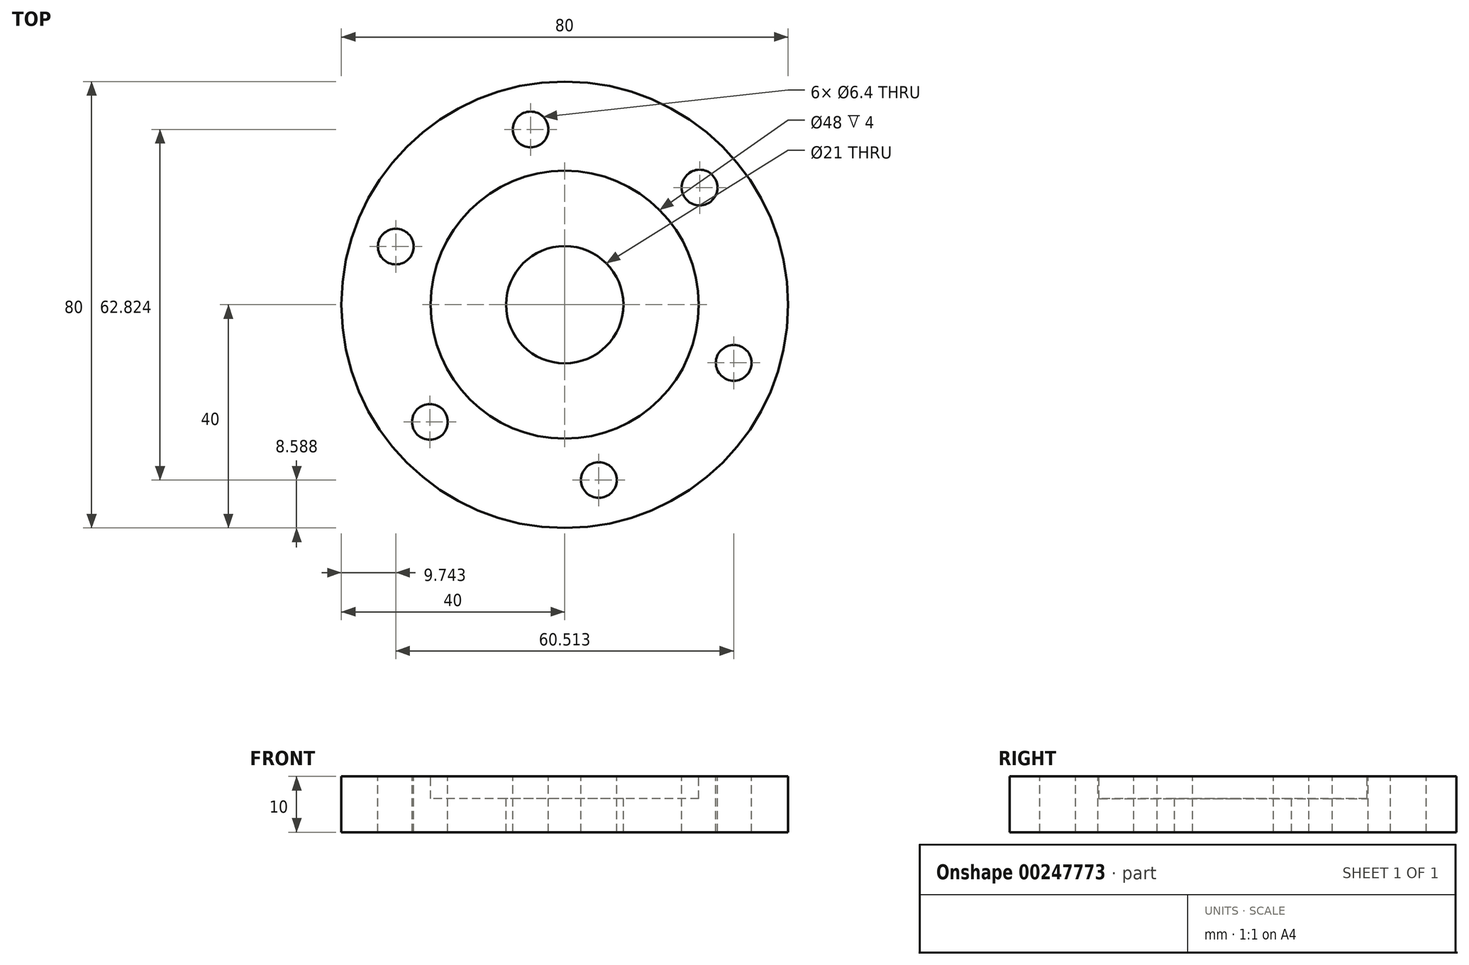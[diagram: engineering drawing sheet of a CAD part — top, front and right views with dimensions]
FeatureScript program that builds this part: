
annotation { "Feature Type Name" : "Feature", "Feature Type Description" : "" }
export const myFeature = defineFeature(function(context is Context, id is Id, definition is map)
    precondition{}
    {
        {
            var Q0;
            Q0=qCreatedBy(makeId("Top.planeOp"),FACE);
            var sketch = newSketch(context, id + "F0", { "sketchPlane" : qUnion([Q0])});
            skCircle(sketch, "E0", {"center": v(0, 0) * mm, "radius": 40 * mm});
            skLineSegment(sketch, "E1", {"start": v(0, 0) * mm, "end": v(-9.46, 48.68) * mm, "construction": true});
            skCircle(sketch, "E2", {"center": v(0, 0) * mm, "radius": 32 * mm, "construction": true});
            skPoint(sketch, "E3", {"position": v(-6.1, 31.41) * mm});
            skPoint(sketch, "E4.1.0", {"position": v(-30.26, 10.42) * mm});
            skPoint(sketch, "E4.2.0", {"position": v(-24.15, -21) * mm});
            skPoint(sketch, "E4.3.0", {"position": v(6.1, -31.41) * mm});
            skPoint(sketch, "E4.4.0", {"position": v(30.26, -10.42) * mm});
            skPoint(sketch, "E4.5.0", {"position": v(24.15, 21) * mm});
            skSolve(sketch);
        }
        {
            var Q0;
            Q0=qSketchRegion(id+"F0",true);
            extrude(context, id + "F1", {"entities" : qUnion([Q0]), "oppositeDirection" : true, "depth" : 10 * mm});
        }
        {
            var Q0;
            Q0=qCreatedBy(makeId("Top.planeOp"),FACE);
            var sketch = newSketch(context, id + "F2", { "sketchPlane" : qUnion([Q0])});
            skCircle(sketch, "E5", {"center": v(0, 0) * mm, "radius": 24 * mm});
            skSolve(sketch);
        }
        {
            var Q0;
            Q0=qSketchRegion(id+"F2",true);
            extrude(context, id + "F3", {"entities" : qUnion([Q0]), "operationType" : NewBodyOperationType.REMOVE, "oppositeDirection" : true, "depth" : 4 * mm, "hasSecondDirection" : true, "secondDirectionOppositeDirection" : false, "secondDirectionDepth" : 10 * mm});
        }
        {
            var Q0;
            Q0=makeQuery(id+"F3.boolean.opBoolean","COPY",FACE,{"derivedFrom":makeQuery(id+"F3.opExtrude","CAP_FACE",FACE,{"disambiguationData":[OSD([sQuery(id+"F2.wireOp",EDGE,"E5")])],"isStart":false})});
            cPlane(context, id + "F4", {"entities" : qUnion([Q0]), "cplaneType" : CPlaneType.OFFSET, "offset" : 0 * mm, "width" : 150 * mm, "height" : 150 * mm});
        }
        {
            var Q0;
            Q0=qCreatedBy(id+"F4.planeOp",FACE);
            var sketch = newSketch(context, id + "F5", { "sketchPlane" : qUnion([Q0])});
            skPoint(sketch, "E6", {"position": v(0, 0) * mm});
            skSolve(sketch);
        }
        {
            var Q0;
            Q0=sQuery(id+"F5.wireOp",VERTEX,"E6");
            var Q1;
            Q1=makeQuery(id+"F1.opExtrude","SWEPT_BODY",BODY,{"disambiguationData":[OSD([sQuery(id+"F0.wireOp",EDGE,"E0")])]});
            hole(context, id + "F6", {"style" : HoleStyle.SIMPLE, "endStyle" : HoleEndStyle.THROUGH, "holeDiameter" : 21 * mm, "locations" : qUnion([Q0]), "scope" : qUnion([Q1]), "isTappedThrough" : true});
        }
        {
            var Q0;
            Q0=sQuery(id+"F0.wireOp",VERTEX,"E3");
            var Q1;
            Q1=sQuery(id+"F0.wireOp",VERTEX,"E4.5.0");
            var Q2;
            Q2=sQuery(id+"F0.wireOp",VERTEX,"E4.4.0");
            var Q3;
            Q3=sQuery(id+"F0.wireOp",VERTEX,"E4.3.0");
            var Q4;
            Q4=sQuery(id+"F0.wireOp",VERTEX,"E4.2.0");
            var Q5;
            Q5=sQuery(id+"F0.wireOp",VERTEX,"E4.1.0");
            var Q6;
            Q6=makeQuery(id+"F1.opExtrude","SWEPT_BODY",BODY,{"disambiguationData":[OSD([sQuery(id+"F0.wireOp",EDGE,"E0")])]});
            hole(context, id + "F7", {"style" : HoleStyle.SIMPLE, "endStyle" : HoleEndStyle.THROUGH, "holeDiameter" : 6.4 * mm, "locations" : qUnion([Q0, Q1, Q2, Q3, Q4, Q5]), "scope" : qUnion([Q6]), "isTappedThrough" : true});
        }
    });
